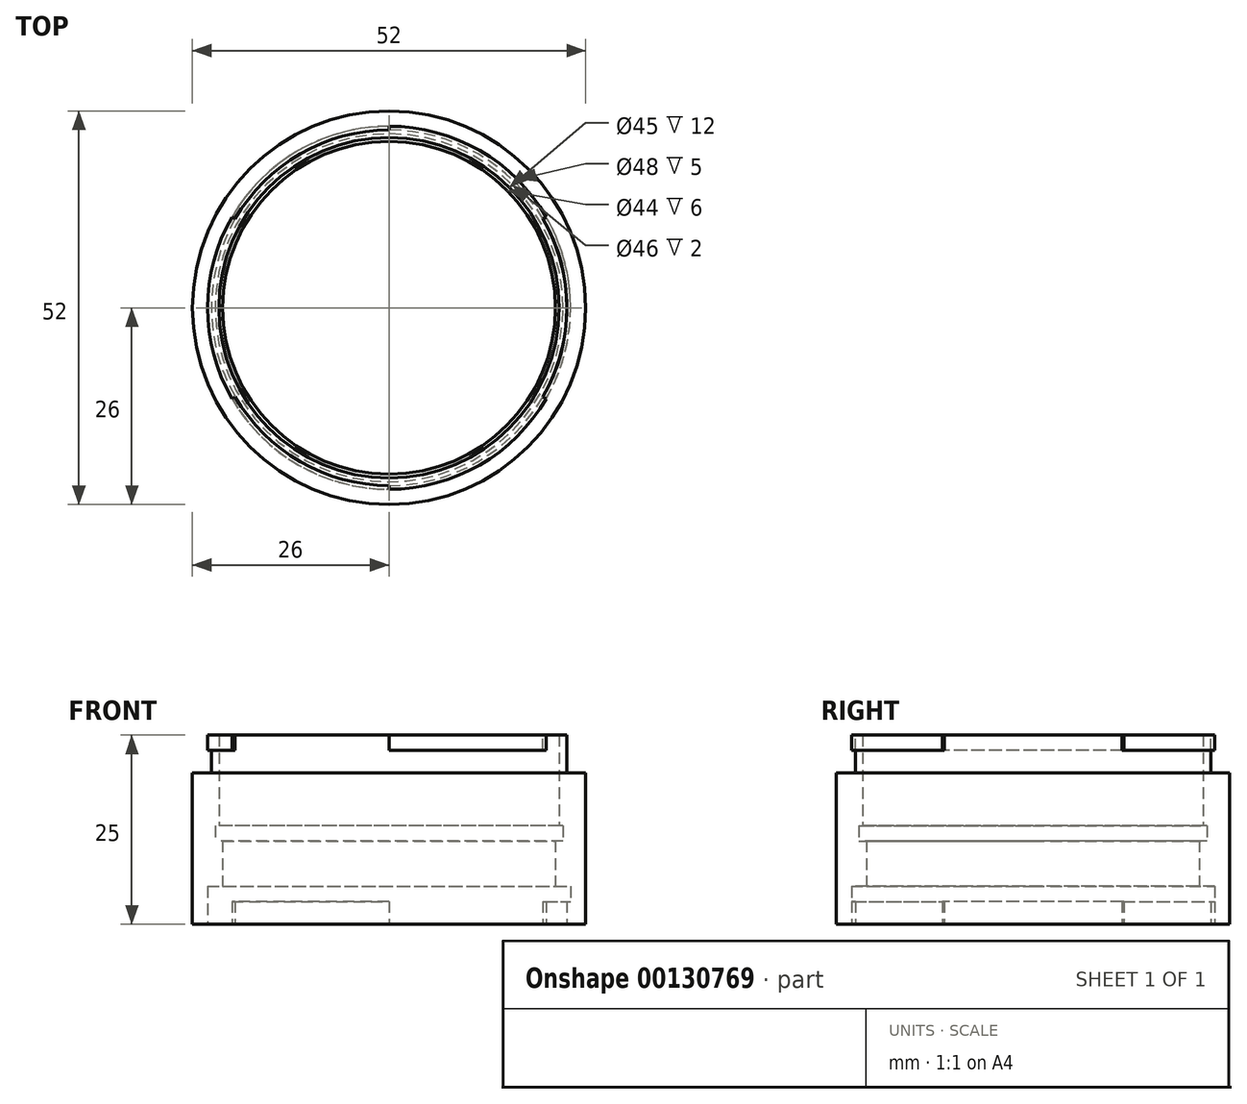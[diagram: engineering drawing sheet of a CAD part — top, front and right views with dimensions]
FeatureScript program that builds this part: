
annotation { "Feature Type Name" : "Feature", "Feature Type Description" : "" }
export const myFeature = defineFeature(function(context is Context, id is Id, definition is map)
    precondition{}
    {
        {
            var Q0;
            Q0=qCreatedBy(makeId("Top.planeOp"),FACE);
            var sketch = newSketch(context, id + "F0", { "sketchPlane" : qUnion([Q0])});
            skCircle(sketch, "E0", {"center": v(0, 0) * mm, "radius": 22.5 * mm});
            skCircle(sketch, "E1", {"center": v(0, 0) * mm, "radius": 26 * mm});
            skSolve(sketch);
        }
        {
            var Q0;
            Q0=makeQuery(id+"F0.imprint","IMPRINT",FACE,{"disambiguationData":[TD([[makeQuery(id+"F0.imprint","IMPRINT",EDGE,{"derivedFrom":sQuery(id+"F0.wireOp",EDGE,"E0")}),-1.0]])]});
            extrude(context, id + "F1", {"entities" : qUnion([Q0]), "depth" : 20 * mm});
        }
        {
            var Q0;
            Q0=makeQuery(id+"F1.opExtrude","CAP_FACE",FACE,{"disambiguationData":[OSD([sQuery(id+"F0.wireOp",EDGE,"E0"),sQuery(id+"F0.wireOp",EDGE,"E1")])],"isStart":true});
            var sketch = newSketch(context, id + "F2", { "sketchPlane" : qUnion([Q0])});
            skCircle(sketch, "E2", {"center": v(0, 0) * mm, "radius": 23.5 * mm});
            skSolve(sketch);
        }
        {
            var Q0;
            Q0=makeQuery(id+"F2.imprint","IMPRINT",FACE,{"disambiguationData":[TD([[makeQuery(id+"F2.imprint","IMPRINT",EDGE,{"derivedFrom":sQuery(id+"F2.wireOp",EDGE,"E2")}),1.0]])]});
            extrude(context, id + "F3", {"entities" : qUnion([Q0]), "operationType" : NewBodyOperationType.REMOVE, "oppositeDirection" : true, "depth" : 5 * mm});
        }
        {
            var Q0;
            Q0=makeQuery(id+"F1.opExtrude","CAP_FACE",FACE,{"disambiguationData":[OSD([sQuery(id+"F0.wireOp",EDGE,"E0"),sQuery(id+"F0.wireOp",EDGE,"E1")])],"isStart":false});
            var sketch = newSketch(context, id + "F4", { "sketchPlane" : qUnion([Q0])});
            skCircle(sketch, "E3", {"center": v(0, 0) * mm, "radius": 23.5 * mm});
            skSolve(sketch);
        }
        {
            var Q0;
            Q0=makeQuery(id+"F4.imprint","IMPRINT",FACE,{"disambiguationData":[TD([[makeQuery(id+"F4.imprint","IMPRINT",EDGE,{"derivedFrom":sQuery(id+"F4.wireOp",EDGE,"E3")}),1.0]])]});
            extrude(context, id + "F5", {"entities" : qUnion([Q0]), "operationType" : NewBodyOperationType.ADD, "depth" : 5 * mm});
        }
        {
            var Q0;
            Q0=makeQuery(id+"F5.opExtrude","CAP_FACE",FACE,{"disambiguationData":[OSD([sQuery(id+"F0.wireOp",EDGE,"E0"),sQuery(id+"F4.wireOp",EDGE,"E3")])],"isStart":false});
            var sketch = newSketch(context, id + "F6", { "sketchPlane" : qUnion([Q0])});
            skCircle(sketch, "E4", {"center": v(0, 0) * mm, "radius": 24 * mm});
            skLineSegment(sketch, "E5", {"start": v(0, 0) * mm, "end": v(0, -24) * mm});
            skLineSegment(sketch, "E6", {"start": v(0, 0) * mm, "end": v(-20.78, -12) * mm});
            skLineSegment(sketch, "E7", {"start": v(0, 0) * mm, "end": v(-20.78, 12) * mm});
            skLineSegment(sketch, "E8", {"start": v(0, 0) * mm, "end": v(0, 24) * mm});
            skLineSegment(sketch, "E9", {"start": v(0, 0) * mm, "end": v(20.78, -12) * mm});
            skLineSegment(sketch, "E10", {"start": v(0, 0) * mm, "end": v(20.78, 12) * mm});
            skSolve(sketch);
        }
        {
            var Q0;
            {var subQ0=sQuery(id+"F6.wireOp",EDGE,"E6");var subQ1=sQuery(id+"F6.wireOp",EDGE,"E4");var subQ2=makeQuery(id+"F6.imprint","INTERSECT",VERTEX,{"derivedFrom":[subQ1,subQ0]});Q0=makeQuery(id+"F6.imprint","IMPRINT",FACE,{"disambiguationData":[TD([[makeQuery(id+"F6.imprint","IMPRINT",EDGE,{"disambiguationData":[TD([[subQ2,1.0]])],"derivedFrom":subQ1}),1.0]])]});}
            var Q1;
            {var subQ0=sQuery(id+"F6.wireOp",EDGE,"E8");var subQ1=sQuery(id+"F6.wireOp",EDGE,"E4");var subQ2=makeQuery(id+"F6.imprint","INTERSECT",VERTEX,{"derivedFrom":[subQ1,subQ0]});Q1=makeQuery(id+"F6.imprint","IMPRINT",FACE,{"disambiguationData":[TD([[makeQuery(id+"F6.imprint","IMPRINT",EDGE,{"disambiguationData":[TD([[subQ2,1.0]])],"derivedFrom":subQ1}),1.0]])]});}
            var Q2;
            {var subQ0=sQuery(id+"F6.wireOp",EDGE,"E5");var subQ1=sQuery(id+"F6.wireOp",EDGE,"E4");var subQ2=makeQuery(id+"F6.imprint","INTERSECT",VERTEX,{"derivedFrom":[subQ1,subQ0]});Q2=makeQuery(id+"F6.imprint","IMPRINT",FACE,{"disambiguationData":[TD([[makeQuery(id+"F6.imprint","IMPRINT",EDGE,{"disambiguationData":[TD([[subQ2,-1.0]])],"derivedFrom":subQ1}),1.0]])]});}
            extrude(context, id + "F7", {"entities" : qUnion([Q0, Q1, Q2]), "operationType" : NewBodyOperationType.ADD, "oppositeDirection" : true, "depth" : 2 * mm});
        }
        {
            var Q0;
            Q0=makeQuery(id+"F1.opExtrude","CAP_FACE",FACE,{"disambiguationData":[OSD([sQuery(id+"F0.wireOp",EDGE,"E0"),sQuery(id+"F0.wireOp",EDGE,"E1")])],"isStart":true});
            var sketch = newSketch(context, id + "F8", { "sketchPlane" : qUnion([Q0])});
            skCircle(sketch, "E11", {"center": v(0, 0) * mm, "radius": 24 * mm});
            skLineSegment(sketch, "E12", {"start": v(0, 0) * mm, "end": v(-20.78, -12) * mm});
            skLineSegment(sketch, "E13", {"start": v(0, 0) * mm, "end": v(-20.78, 12) * mm});
            skLineSegment(sketch, "E14", {"start": v(0, 0) * mm, "end": v(0, 24) * mm});
            skLineSegment(sketch, "E15", {"start": v(0, 0) * mm, "end": v(20.78, 12) * mm});
            skLineSegment(sketch, "E16", {"start": v(0, 0) * mm, "end": v(20.78, -12) * mm});
            skLineSegment(sketch, "E17", {"start": v(0, 0) * mm, "end": v(0, -24) * mm});
            skSolve(sketch);
        }
        {
            var Q0;
            {var subQ0=sQuery(id+"F8.wireOp",EDGE,"E14");var subQ1=sQuery(id+"F8.wireOp",EDGE,"E11");var subQ2=makeQuery(id+"F8.imprint","INTERSECT",VERTEX,{"derivedFrom":[subQ1,subQ0]});Q0=makeQuery(id+"F8.imprint","IMPRINT",FACE,{"disambiguationData":[TD([[makeQuery(id+"F8.imprint","IMPRINT",EDGE,{"disambiguationData":[TD([[subQ2,1.0]])],"derivedFrom":subQ1}),1.0]])]});}
            var Q1;
            {var subQ0=sQuery(id+"F8.wireOp",EDGE,"E16");var subQ1=sQuery(id+"F8.wireOp",EDGE,"E11");var subQ2=makeQuery(id+"F8.imprint","INTERSECT",VERTEX,{"derivedFrom":[subQ1,subQ0]});Q1=makeQuery(id+"F8.imprint","IMPRINT",FACE,{"disambiguationData":[TD([[makeQuery(id+"F8.imprint","IMPRINT",EDGE,{"disambiguationData":[TD([[subQ2,1.0]])],"derivedFrom":subQ1}),1.0]])]});}
            var Q2;
            {var subQ0=sQuery(id+"F8.wireOp",EDGE,"E12");var subQ1=sQuery(id+"F8.wireOp",EDGE,"E11");var subQ2=makeQuery(id+"F8.imprint","INTERSECT",VERTEX,{"derivedFrom":[subQ1,subQ0]});Q2=makeQuery(id+"F8.imprint","IMPRINT",FACE,{"disambiguationData":[TD([[makeQuery(id+"F8.imprint","IMPRINT",EDGE,{"disambiguationData":[TD([[subQ2,1.0]])],"derivedFrom":subQ1}),1.0]])]});}
            extrude(context, id + "F9", {"entities" : qUnion([Q0, Q1, Q2]), "operationType" : NewBodyOperationType.REMOVE, "oppositeDirection" : true, "depth" : 5 * mm});
        }
        {
            var Q0;
            Q0=makeQuery(id+"F3.boolean.opBoolean","COPY",FACE,{"derivedFrom":makeQuery(id+"F3.opExtrude","CAP_FACE",FACE,{"disambiguationData":[OSD([sQuery(id+"F0.wireOp",EDGE,"E0"),sQuery(id+"F2.wireOp",EDGE,"E2")])],"isStart":false})});
            var sketch = newSketch(context, id + "F10", { "sketchPlane" : qUnion([Q0])});
            skCircle(sketch, "E18", {"center": v(0, 0) * mm, "radius": 23.5 * mm});
            skCircle(sketch, "E19", {"center": v(0, 0) * mm, "radius": 24 * mm});
            skSolve(sketch);
        }
        {
            var Q0;
            {var subQ1=makeQuery(id+"F9.boolean.opBoolean","COPY",EDGE,{"derivedFrom":makeQuery(id+"F9.opExtrude","CAP_EDGE",EDGE,{"disambiguationData":[OSD([sQuery(id+"F8.wireOp",EDGE,"E15")])],"isStart":false})});Q0=makeQuery(id+"F10.imprint","IMPRINT",FACE,{"disambiguationData":[TD([[makeQuery(id+"F10.imprint","IMPRINT",EDGE,{"derivedFrom":subQ1}),-1.0]])]});}
            var Q1;
            {var subQ1=makeQuery(id+"F9.boolean.opBoolean","COPY",EDGE,{"derivedFrom":makeQuery(id+"F9.opExtrude","CAP_EDGE",EDGE,{"disambiguationData":[OSD([sQuery(id+"F8.wireOp",EDGE,"E12")])],"isStart":false})});Q1=makeQuery(id+"F10.imprint","IMPRINT",FACE,{"disambiguationData":[TD([[makeQuery(id+"F10.imprint","IMPRINT",EDGE,{"derivedFrom":subQ1}),1.0]])]});}
            var Q2;
            {var subQ1=makeQuery(id+"F9.boolean.opBoolean","COPY",EDGE,{"derivedFrom":makeQuery(id+"F9.opExtrude","CAP_EDGE",EDGE,{"disambiguationData":[OSD([sQuery(id+"F8.wireOp",EDGE,"E13")])],"isStart":false})});Q2=makeQuery(id+"F10.imprint","IMPRINT",FACE,{"disambiguationData":[TD([[makeQuery(id+"F10.imprint","IMPRINT",EDGE,{"derivedFrom":subQ1}),-1.0]])]});}
            extrude(context, id + "F11", {"entities" : qUnion([Q0, Q1, Q2]), "operationType" : NewBodyOperationType.REMOVE, "depth" : 2 * mm});
        }
        {
            var Q0;
            {var subQ0=sQuery(id+"F10.wireOp",EDGE,"E19");var subQ1=sQuery(id+"F10.wireOp",EDGE,"E18");var subQ2=sQuery(id+"F8.wireOp",EDGE,"E16");var subQ3=sQuery(id+"F8.wireOp",EDGE,"E15");var subQ4=sQuery(id+"F8.wireOp",EDGE,"E17");var subQ5=sQuery(id+"F8.wireOp",EDGE,"E12");var subQ6=sQuery(id+"F8.wireOp",EDGE,"E14");var subQ7=sQuery(id+"F8.wireOp",EDGE,"E13");var subQ8=sQuery(id+"F8.wireOp",EDGE,"E11");var subQ9=sQuery(id+"F2.wireOp",EDGE,"E2");Q0=makeQuery(id+"F11.boolean.opBoolean","MERGE",FACE,{"derivedFrom":[makeQuery(id+"F9.boolean.opBoolean","MERGE",FACE,{"derivedFrom":[makeQuery(id+"F3.boolean.opBoolean","COPY",FACE,{"derivedFrom":makeQuery(id+"F3.opExtrude","CAP_FACE",FACE,{"disambiguationData":[OSD([sQuery(id+"F0.wireOp",EDGE,"E0"),subQ9])],"isStart":false})}),makeQuery(id+"F9.opExtrude","CAP_FACE",FACE,{"disambiguationData":[OSD([subQ9,subQ8,subQ6,subQ3])],"isStart":false}),makeQuery(id+"F9.opExtrude","CAP_FACE",FACE,{"disambiguationData":[OSD([subQ9,subQ8,subQ5,subQ7])],"isStart":false}),makeQuery(id+"F9.opExtrude","CAP_FACE",FACE,{"disambiguationData":[OSD([subQ9,subQ8,subQ2,subQ4])],"isStart":false})]}),makeQuery(id+"F11.opExtrude","CAP_FACE",FACE,{"disambiguationData":[OSD([subQ7,subQ6,subQ1,subQ0])],"isStart":true}),makeQuery(id+"F11.opExtrude","CAP_FACE",FACE,{"disambiguationData":[OSD([subQ5,subQ4,subQ1,subQ0])],"isStart":true}),makeQuery(id+"F11.opExtrude","CAP_FACE",FACE,{"disambiguationData":[OSD([subQ3,subQ2,subQ1,subQ0])],"isStart":true})]});}
            var sketch = newSketch(context, id + "F12", { "sketchPlane" : qUnion([Q0])});
            skCircle(sketch, "E20", {"center": v(0, 0) * mm, "radius": 22.5 * mm});
            skCircle(sketch, "E21", {"center": v(0, 0) * mm, "radius": 22 * mm});
            skSolve(sketch);
        }
        {
            var Q0;
            Q0=makeQuery(id+"F12.imprint","IMPRINT",FACE,{"disambiguationData":[TD([[makeQuery(id+"F12.imprint","IMPRINT",EDGE,{"derivedFrom":sQuery(id+"F12.wireOp",EDGE,"E20")}),-1.0]])]});
            extrude(context, id + "F13", {"entities" : qUnion([Q0]), "operationType" : NewBodyOperationType.ADD, "oppositeDirection" : true, "depth" : 6 * mm});
        }
        {
            var Q0;
            Q0=makeQuery(id+"F13.opExtrude","CAP_FACE",FACE,{"disambiguationData":[OSD([sQuery(id+"F12.wireOp",EDGE,"E20"),sQuery(id+"F12.wireOp",EDGE,"E21")])],"isStart":false});
            var sketch = newSketch(context, id + "F14", { "sketchPlane" : qUnion([Q0])});
            skCircle(sketch, "E22", {"center": v(0, 0) * mm, "radius": 23 * mm});
            skCircle(sketch, "E23", {"center": v(0, 0) * mm, "radius": 22.5 * mm});
            skSolve(sketch);
        }
        {
            var Q0;
            Q0=makeQuery(id+"F14.imprint","IMPRINT",FACE,{"disambiguationData":[TD([[makeQuery(id+"F14.imprint","IMPRINT",EDGE,{"derivedFrom":sQuery(id+"F14.wireOp",EDGE,"E22")}),1.0]])]});
            extrude(context, id + "F15", {"entities" : qUnion([Q0]), "operationType" : NewBodyOperationType.REMOVE, "depth" : 2 * mm});
        }
    });
